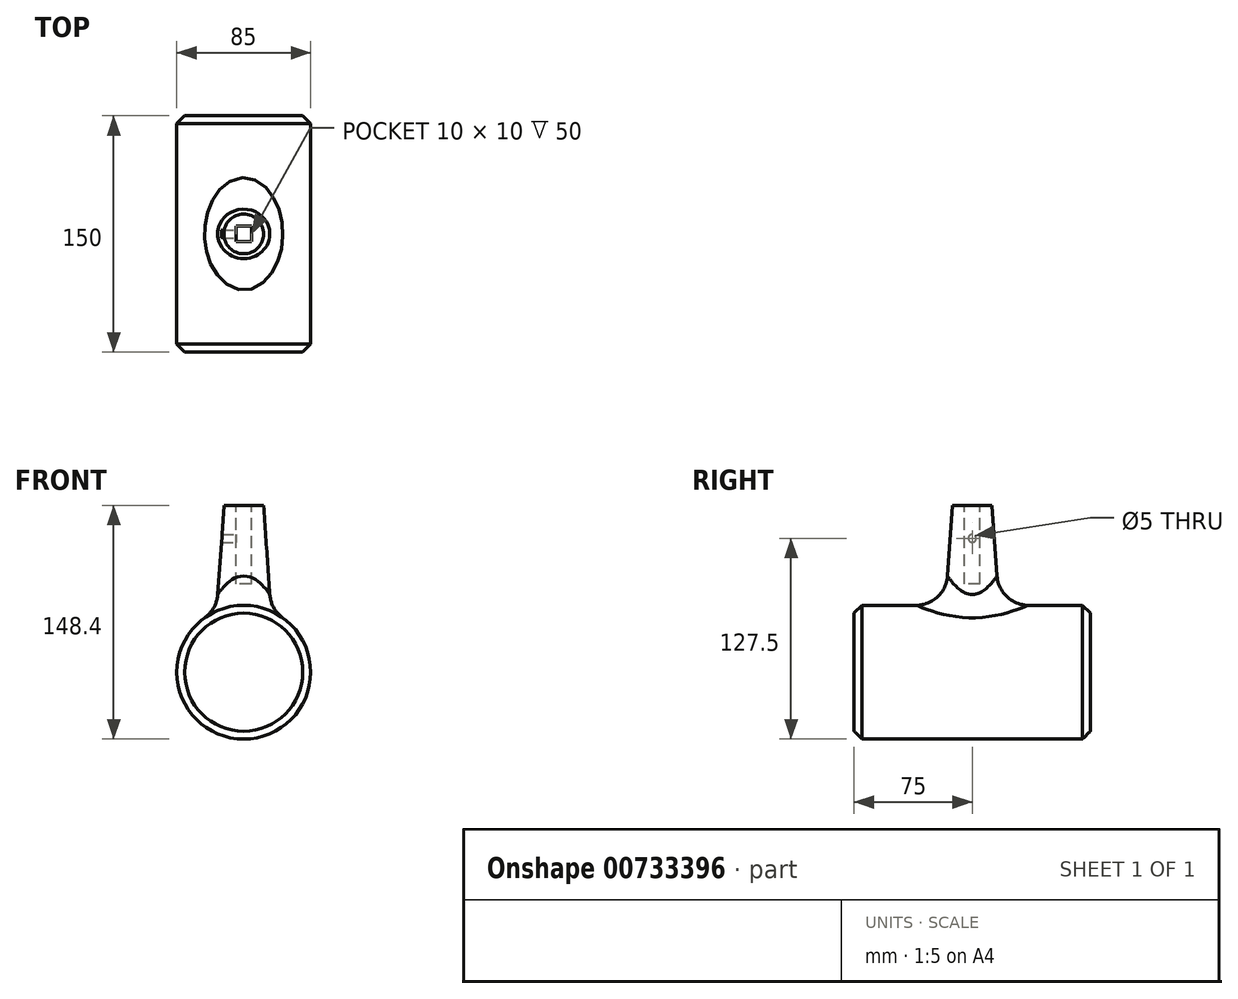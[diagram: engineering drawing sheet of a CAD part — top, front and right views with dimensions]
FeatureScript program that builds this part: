
annotation { "Feature Type Name" : "Feature", "Feature Type Description" : "" }
export const myFeature = defineFeature(function(context is Context, id is Id, definition is map)
    precondition{}
    {
        {
            var Q0;
            Q0=qCreatedBy(makeId("Front.planeOp"),FACE);
            var sketch = newSketch(context, id + "F0", { "sketchPlane" : qUnion([Q0])});
            skCircle(sketch, "E0", {"center": v(0, 0) * mm, "radius": 42.5 * mm});
            skSolve(sketch);
        }
        {
            var Q0;
            Q0=makeQuery(id+"F0.imprint","IMPRINT",FACE,{"disambiguationData":[TD([[makeQuery(id+"F0.imprint","IMPRINT",EDGE,{"derivedFrom":sQuery(id+"F0.wireOp",EDGE,"E0")}),1.0]])]});
            extrude(context, id + "F1", {"entities" : qUnion([Q0]), "endBound" : BoundingType.SYMMETRIC, "depth" : 150 * mm, "offsetDistance" : 25 * mm});
        }
        {
            var Q0;
            Q0=qCreatedBy(makeId("Top.planeOp"),FACE);
            var sketch = newSketch(context, id + "F2", { "sketchPlane" : qUnion([Q0])});
            skCircle(sketch, "E1", {"center": v(0, 0) * mm, "radius": 20 * mm});
            skSolve(sketch);
        }
        {
            var Q0;
            Q0 = qSketchRegion(id + "F2", true);
            extrude(context, id + "F3", {"entities" : qUnion([Q0]), "operationType" : NewBodyOperationType.ADD, "depth" : 105.9 * mm, "offsetDistance" : 25 * mm, "hasDraft" : true, "draftAngle" : 4 * degree, "draftPullDirection" : true});
        }
        {
            var Q0;
            Q0=makeQuery(id+"F3.opExtrude","CAP_FACE",FACE,{"disambiguationData":[OSD([sQuery(id+"F2.wireOp",EDGE,"E1")])],"isStart":false});
            var sketch = newSketch(context, id + "F4", { "sketchPlane" : qUnion([Q0])});
            skLineSegment(sketch, "E2.bottom", {"start": v(5, 5) * mm, "end": v(-5, 5) * mm});
            skLineSegment(sketch, "E2.top", {"start": v(5, -5) * mm, "end": v(-5, -5) * mm});
            skLineSegment(sketch, "E2.left", {"start": v(5, 5) * mm, "end": v(5, -5) * mm});
            skLineSegment(sketch, "E2.right", {"start": v(-5, 5) * mm, "end": v(-5, -5) * mm});
            skPoint(sketch, "E2.middle", {"position": v(0, 0) * mm});
            skSolve(sketch);
        }
        {
            var Q0;
            Q0 = qSketchRegion(id + "F4", true);
            extrude(context, id + "F5", {"entities" : qUnion([Q0]), "operationType" : NewBodyOperationType.REMOVE, "oppositeDirection" : true, "depth" : 50 * mm, "offsetDistance" : 25 * mm});
        }
        {
            var Q0;
            Q0=qCreatedBy(makeId("Right.planeOp"),FACE);
            var sketch = newSketch(context, id + "F6", { "sketchPlane" : qUnion([Q0])});
            skCircle(sketch, "E3", {"center": v(0, 85) * mm, "radius": 2.5 * mm});
            skSolve(sketch);
        }
        {
            var Q0;
            Q0 = qSketchRegion(id + "F6", true);
            extrude(context, id + "F7", {"entities" : qUnion([Q0]), "operationType" : NewBodyOperationType.REMOVE, "oppositeDirection" : true, "depth" : 50 * mm, "offsetDistance" : 25 * mm});
        }
        {
            var Q0;
            Q0=makeQuery(id+"F1.opExtrude","CAP_EDGE",EDGE,{"disambiguationData":[OSD([sQuery(id+"F0.wireOp",EDGE,"E0")])],"isStart":false});
            var Q1;
            Q1=makeQuery(id+"F1.opExtrude","CAP_EDGE",EDGE,{"disambiguationData":[OSD([sQuery(id+"F0.wireOp",EDGE,"E0")])],"isStart":true});
            chamfer(context, id + "F8", {"entities" : qUnion([Q0, Q1]), "width" : 5 * mm, "tangentPropagation" : true});
        }
        {
            var Q0;
            Q0=makeQuery(id+"F3.boolean.opBoolean","INTERSECT",EDGE,{"derivedFrom":[makeQuery(id+"F1.opExtrude","SWEPT_FACE",FACE,{"disambiguationData":[OSD([sQuery(id+"F0.wireOp",EDGE,"E0")])]}),makeQuery(id+"F3.opExtrude","SWEPT_FACE",FACE,{"disambiguationData":[OSD([sQuery(id+"F2.wireOp",EDGE,"E1")])]})]});
            fillet(context, id + "F9", {"entities" : qUnion([Q0]), "radius" : 20 * mm, "tangentPropagation" : true, "allowEdgeOverflow" : false});
        }
    });
